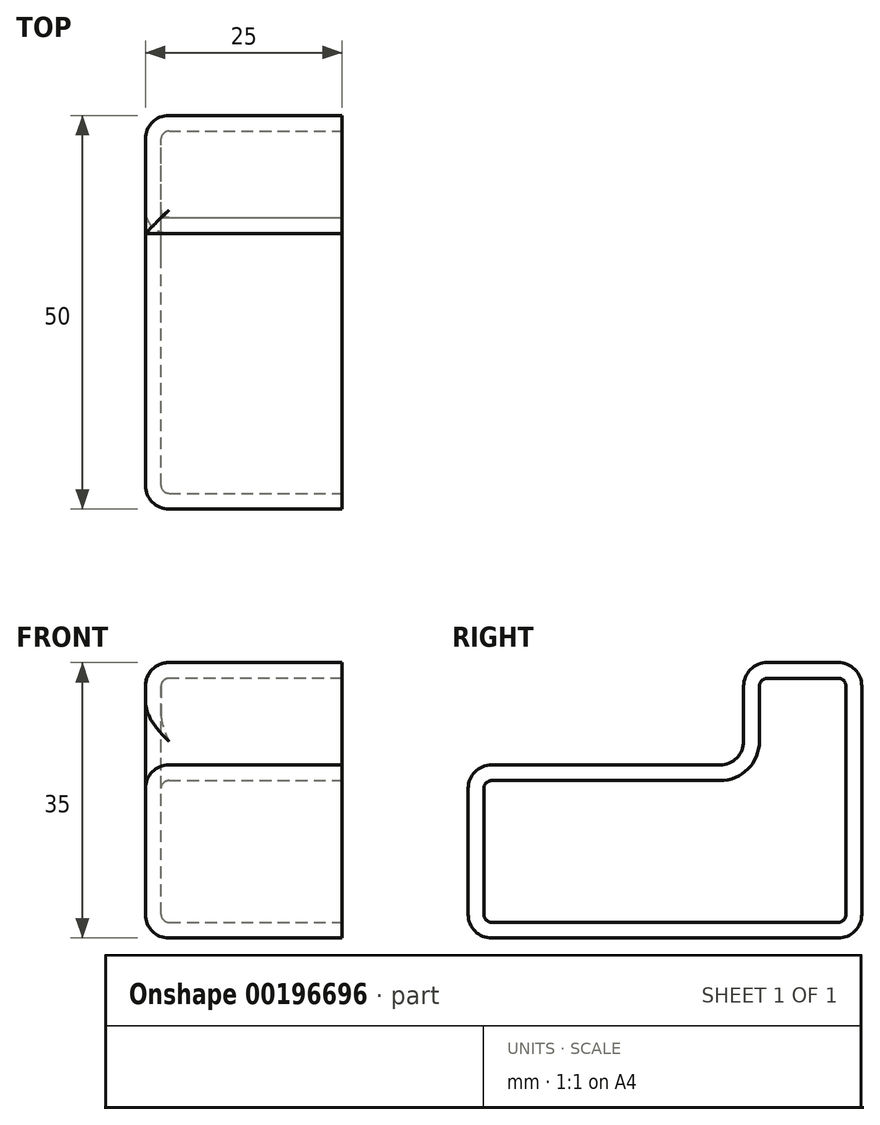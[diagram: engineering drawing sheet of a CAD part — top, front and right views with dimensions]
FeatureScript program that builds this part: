
annotation { "Feature Type Name" : "Feature", "Feature Type Description" : "" }
export const myFeature = defineFeature(function(context is Context, id is Id, definition is map)
    precondition{}
    {
        {
            var Q0;
            Q0=qCreatedBy(makeId("Right.planeOp"),FACE);
            var sketch = newSketch(context, id + "F0", { "sketchPlane" : qUnion([Q0])});
            skLineSegment(sketch, "E0", {"start": v(0, 14.42) * mm, "end": v(-35, 14.42) * mm});
            skLineSegment(sketch, "E1", {"start": v(-35, -7.58) * mm, "end": v(15, -7.58) * mm});
            skLineSegment(sketch, "E2", {"start": v(15, -7.58) * mm, "end": v(15, 27.42) * mm});
            skLineSegment(sketch, "E3", {"start": v(15, 27.42) * mm, "end": v(0, 27.42) * mm});
            skLineSegment(sketch, "E4", {"start": v(0, 27.42) * mm, "end": v(0, 14.42) * mm});
            skLineSegment(sketch, "E5", {"start": v(-35, 14.42) * mm, "end": v(-35, -7.58) * mm});
            skSolve(sketch);
        }
        {
            var Q0;
            Q0=makeQuery(id+"F0.imprint","IMPRINT",FACE,{"disambiguationData":[TD([[makeQuery(id+"F0.imprint","IMPRINT",EDGE,{"derivedFrom":sQuery(id+"F0.wireOp",EDGE,"E0")}),1.0]])]});
            extrude(context, id + "F1", {"entities" : qUnion([Q0]), "depth" : 25 * mm});
        }
        {
            var Q0;
            Q0=makeQuery(id+"F1.opExtrude","CAP_EDGE",EDGE,{"disambiguationData":[OSD([sQuery(id+"F0.wireOp",EDGE,"E1")])],"isStart":true});
            var Q1;
            Q1=makeQuery(id+"F1.opExtrude","CAP_EDGE",EDGE,{"disambiguationData":[OSD([sQuery(id+"F0.wireOp",EDGE,"E5")])],"isStart":true});
            var Q2;
            Q2=makeQuery(id+"F1.opExtrude","CAP_EDGE",EDGE,{"disambiguationData":[OSD([sQuery(id+"F0.wireOp",EDGE,"E0")])],"isStart":true});
            var Q3;
            Q3=makeQuery(id+"F1.opExtrude","CAP_EDGE",EDGE,{"disambiguationData":[OSD([sQuery(id+"F0.wireOp",EDGE,"E3")])],"isStart":true});
            var Q4;
            Q4=makeQuery(id+"F1.opExtrude","CAP_EDGE",EDGE,{"disambiguationData":[OSD([sQuery(id+"F0.wireOp",EDGE,"E2")])],"isStart":true});
            var Q5;
            Q5=makeQuery(id+"F1.opExtrude","SWEPT_EDGE",EDGE,{"disambiguationData":[OSD([sQuery(id+"F0.wireOp",EDGE,"E1"),sQuery(id+"F0.wireOp",EDGE,"E2")])]});
            var Q6;
            Q6=makeQuery(id+"F1.opExtrude","SWEPT_EDGE",EDGE,{"disambiguationData":[OSD([sQuery(id+"F0.wireOp",EDGE,"E1"),sQuery(id+"F0.wireOp",EDGE,"E5")])]});
            var Q7;
            Q7=makeQuery(id+"F1.opExtrude","SWEPT_EDGE",EDGE,{"disambiguationData":[OSD([sQuery(id+"F0.wireOp",EDGE,"E0"),sQuery(id+"F0.wireOp",EDGE,"E5")])]});
            var Q8;
            Q8=makeQuery(id+"F1.opExtrude","SWEPT_EDGE",EDGE,{"disambiguationData":[OSD([sQuery(id+"F0.wireOp",EDGE,"E0"),sQuery(id+"F0.wireOp",EDGE,"E4")])]});
            var Q9;
            Q9=makeQuery(id+"F1.opExtrude","SWEPT_EDGE",EDGE,{"disambiguationData":[OSD([sQuery(id+"F0.wireOp",EDGE,"E3"),sQuery(id+"F0.wireOp",EDGE,"E4")])]});
            var Q10;
            Q10=makeQuery(id+"F1.opExtrude","SWEPT_EDGE",EDGE,{"disambiguationData":[OSD([sQuery(id+"F0.wireOp",EDGE,"E2"),sQuery(id+"F0.wireOp",EDGE,"E3")])]});
            fillet(context, id + "F2", {"entities" : qUnion([Q0, Q1, Q2, Q3, Q4, Q5, Q6, Q7, Q8, Q9, Q10]), "radius" : 3 * mm, "tangentPropagation" : true, "allowEdgeOverflow" : false});
        }
        {
            var Q0;
            Q0=makeQuery(id+"F1.opExtrude","CAP_FACE",FACE,{"disambiguationData":[OSD([sQuery(id+"F0.wireOp",EDGE,"E0"),sQuery(id+"F0.wireOp",EDGE,"E1"),sQuery(id+"F0.wireOp",EDGE,"E2"),sQuery(id+"F0.wireOp",EDGE,"E3"),sQuery(id+"F0.wireOp",EDGE,"E4"),sQuery(id+"F0.wireOp",EDGE,"E5")])],"isStart":false});
            shell(context, id + "F3", {"entities" : qUnion([Q0]), "thickness" : 2 * mm});
        }
    });
